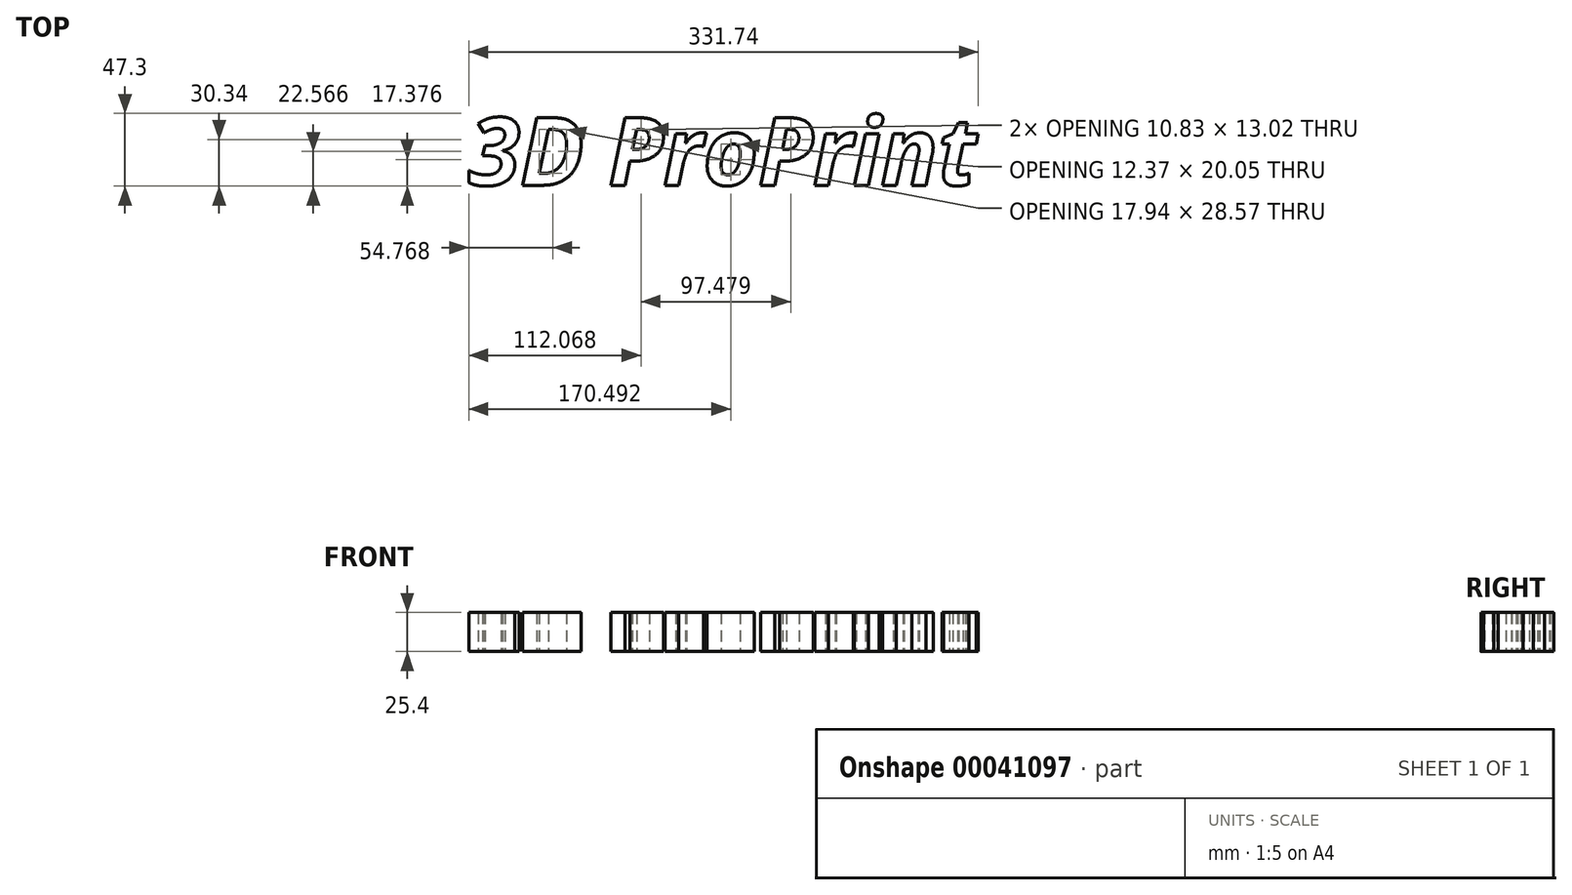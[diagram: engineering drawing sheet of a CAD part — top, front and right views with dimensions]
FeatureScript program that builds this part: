
annotation { "Feature Type Name" : "Feature", "Feature Type Description" : "" }
export const myFeature = defineFeature(function(context is Context, id is Id, definition is map)
    precondition{}
    {
        {
            var Q0;
            Q0=qCreatedBy(makeId("Top.planeOp"),FACE);
            var sketch = newSketch(context, id + "F0", { "sketchPlane" : qUnion([Q0])});
            skText(sketch, "E0", { "text": "3D ProPrint", "fontName": "OpenSans-BoldItalic.ttf"});
            const initialGuessF0  = {"E0": [-0.06889, -0.01017, 1, 0, 0.04425]};
            skSetInitialGuess(sketch, initialGuessF0);
            skSolve(sketch);
        }
        {
            var Q0;
            Q0=makeQuery(id+"F0.imprint","IMPRINT",FACE,{"disambiguationData":[TD([[makeQuery(id+"F0.imprint","IMPRINT",EDGE,{"derivedFrom":sQuery(id+"F0.wireOp",EDGE,"E0.sketch_text.stroke-0")}),-1.0]])]});
            var Q1;
            Q1=makeQuery(id+"F0.imprint","IMPRINT",FACE,{"disambiguationData":[TD([[makeQuery(id+"F0.imprint","IMPRINT",EDGE,{"derivedFrom":sQuery(id+"F0.wireOp",EDGE,"E0.sketch_text.stroke-59")}),-1.0]])]});
            var Q2;
            Q2=makeQuery(id+"F0.imprint","IMPRINT",FACE,{"disambiguationData":[TD([[makeQuery(id+"F0.imprint","IMPRINT",EDGE,{"derivedFrom":sQuery(id+"F0.wireOp",EDGE,"E0.sketch_text.stroke-104")}),-1.0]])]});
            var Q3;
            Q3=makeQuery(id+"F0.imprint","IMPRINT",FACE,{"disambiguationData":[TD([[makeQuery(id+"F0.imprint","IMPRINT",EDGE,{"derivedFrom":sQuery(id+"F0.wireOp",EDGE,"E0.sketch_text.stroke-116")}),-1.0]])]});
            var Q4;
            Q4=makeQuery(id+"F0.imprint","IMPRINT",FACE,{"disambiguationData":[TD([[makeQuery(id+"F0.imprint","IMPRINT",EDGE,{"derivedFrom":sQuery(id+"F0.wireOp",EDGE,"E0.sketch_text.stroke-123")}),-1.0]])]});
            var Q5;
            Q5=makeQuery(id+"F0.imprint","IMPRINT",FACE,{"disambiguationData":[TD([[makeQuery(id+"F0.imprint","IMPRINT",EDGE,{"derivedFrom":sQuery(id+"F0.wireOp",EDGE,"E0.sketch_text.stroke-127")}),-1.0]])]});
            var Q6;
            Q6=makeQuery(id+"F0.imprint","IMPRINT",FACE,{"disambiguationData":[TD([[makeQuery(id+"F0.imprint","IMPRINT",EDGE,{"derivedFrom":sQuery(id+"F0.wireOp",EDGE,"E0.sketch_text.stroke-144")}),-1.0]])]});
            var Q7;
            Q7=makeQuery(id+"F0.imprint","IMPRINT",FACE,{"disambiguationData":[TD([[makeQuery(id+"F0.imprint","IMPRINT",EDGE,{"derivedFrom":sQuery(id+"F0.wireOp",EDGE,"E0.sketch_text.stroke-28")}),-1.0]])]});
            var Q8;
            Q8=makeQuery(id+"F0.imprint","IMPRINT",FACE,{"disambiguationData":[TD([[makeQuery(id+"F0.imprint","IMPRINT",EDGE,{"derivedFrom":sQuery(id+"F0.wireOp",EDGE,"E0.sketch_text.stroke-44")}),-1.0]])]});
            var Q9;
            Q9=makeQuery(id+"F0.imprint","IMPRINT",FACE,{"disambiguationData":[TD([[makeQuery(id+"F0.imprint","IMPRINT",EDGE,{"derivedFrom":sQuery(id+"F0.wireOp",EDGE,"E0.sketch_text.stroke-71")}),-1.0]])]});
            var Q10;
            Q10=makeQuery(id+"F0.imprint","IMPRINT",FACE,{"disambiguationData":[TD([[makeQuery(id+"F0.imprint","IMPRINT",EDGE,{"derivedFrom":sQuery(id+"F0.wireOp",EDGE,"E0.sketch_text.stroke-89")}),-1.0]])]});
            extrude(context, id + "F1", {"entities" : qUnion([Q0, Q1, Q2, Q3, Q4, Q5, Q6, Q7, Q8, Q9, Q10]), "depth" : 25.4 * mm});
        }
    });
